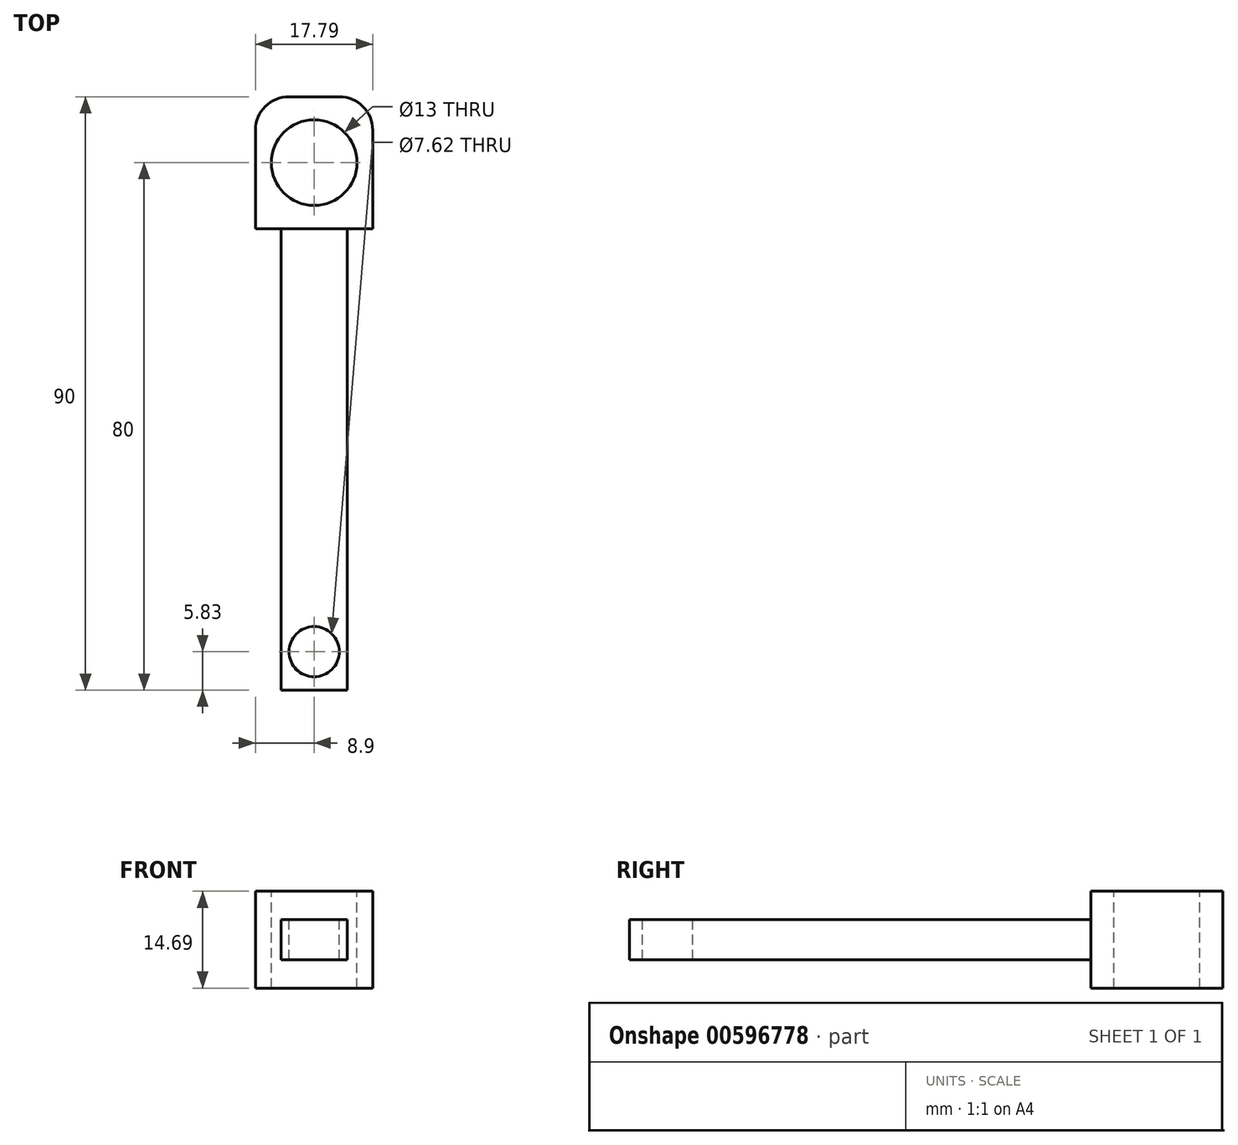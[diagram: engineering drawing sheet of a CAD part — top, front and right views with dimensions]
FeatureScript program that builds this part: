
annotation { "Feature Type Name" : "Feature", "Feature Type Description" : "" }
export const myFeature = defineFeature(function(context is Context, id is Id, definition is map)
    precondition{}
    {
        {
            var Q0;
            Q0=qCreatedBy(makeId("Top.planeOp"),FACE);
            var sketch = newSketch(context, id + "F0", { "sketchPlane" : qUnion([Q0])});
            skLineSegment(sketch, "E0.bottom", {"start": v(5, -35) * mm, "end": v(-5, -35) * mm});
            skLineSegment(sketch, "E0.top", {"start": v(5, 35) * mm, "end": v(-5, 35) * mm});
            skLineSegment(sketch, "E0.left", {"start": v(5, -35) * mm, "end": v(5, 35) * mm});
            skLineSegment(sketch, "E0.right", {"start": v(-5, -35) * mm, "end": v(-5, 35) * mm});
            skPoint(sketch, "E0.middle", {"position": v(0, 0) * mm});
            skPoint(sketch, "E1.firstSnap0", {"position": v(0, 35) * mm});
            skLineSegment(sketch, "E1.bottom", {"start": v(-8.9, 35) * mm, "end": v(8.89, 35) * mm});
            skLineSegment(sketch, "E1.top", {"start": v(-8.9, 55) * mm, "end": v(8.89, 55) * mm});
            skLineSegment(sketch, "E1.left", {"start": v(-8.9, 35) * mm, "end": v(-8.9, 55) * mm});
            skLineSegment(sketch, "E1.right", {"start": v(8.89, 35) * mm, "end": v(8.89, 55) * mm});
            skSolve(sketch);
        }
        {
            var Q0;
            Q0=makeQuery(id+"F0.imprint","IMPRINT",FACE,{"disambiguationData":[TD([[makeQuery(id+"F0.imprint","IMPRINT",EDGE,{"derivedFrom":sQuery(id+"F0.wireOp",EDGE,"E1.top")}),-1.0]])]});
            var Q1;
            Q1=makeQuery(id+"F0.imprint","IMPRINT",FACE,{"disambiguationData":[TD([[makeQuery(id+"F0.imprint","IMPRINT",EDGE,{"derivedFrom":sQuery(id+"F0.wireOp",EDGE,"E0.bottom")}),-1.0]])]});
            extrude(context, id + "F1", {"entities" : qUnion([Q0, Q1]), "depth" : 14.7 * mm, "offsetDistance" : 25.4 * mm});
        }
        {
            var Q0;
            Q0=makeQuery(id+"F1.opExtrude","SWEPT_FACE",FACE,{"disambiguationData":[OSD([sQuery(id+"F0.wireOp",EDGE,"E0.bottom")])]});
            var sketch = newSketch(context, id + "F2", { "sketchPlane" : qUnion([Q0])});
            skLineSegment(sketch, "E2.bottom", {"start": v(-5, 10.4) * mm, "end": v(5, 10.4) * mm});
            skLineSegment(sketch, "E2.top", {"start": v(-5, 4.29) * mm, "end": v(5, 4.29) * mm});
            skLineSegment(sketch, "E2.left", {"start": v(-5, 10.4) * mm, "end": v(-5, 4.29) * mm});
            skLineSegment(sketch, "E2.right", {"start": v(5, 10.4) * mm, "end": v(5, 4.29) * mm});
            skPoint(sketch, "E2.middle", {"position": v(0, 7.34) * mm});
            skPoint(sketch, "E2.middle.positionSnap0", {"position": v(-5, 7.34) * mm});
            skPoint(sketch, "E2.centerSnap0", {"position": v(-5, 7.34) * mm});
            skSolve(sketch);
        }
        {
            var Q0;
            {var subQ0=sQuery(id+"F2.wireOp",EDGE,"E2.bottom");Q0=makeQuery(id+"F2.imprint","IMPRINT",FACE,{"disambiguationData":[TD([[makeQuery(id+"F2.imprint","IMPRINT",EDGE,{"derivedFrom":subQ0}),1.0]])]});}
            var Q1;
            {var subQ0=sQuery(id+"F2.wireOp",EDGE,"E2.top");Q1=makeQuery(id+"F2.imprint","IMPRINT",FACE,{"disambiguationData":[TD([[makeQuery(id+"F2.imprint","IMPRINT",EDGE,{"derivedFrom":subQ0}),-1.0]])]});}
            extrude(context, id + "F3", {"entities" : qUnion([Q0, Q1]), "operationType" : NewBodyOperationType.REMOVE, "oppositeDirection" : true, "depth" : 70 * mm, "offsetDistance" : 25.4 * mm});
        }
        {
            var Q0;
            Q0=makeQuery(id+"F1.opExtrude","CAP_FACE",FACE,{"disambiguationData":[OSD([sQuery(id+"F0.wireOp",EDGE,"E0.bottom"),sQuery(id+"F0.wireOp",EDGE,"E0.left"),sQuery(id+"F0.wireOp",EDGE,"E0.right"),sQuery(id+"F0.wireOp",EDGE,"E1.bottom"),sQuery(id+"F0.wireOp",EDGE,"E1.top"),sQuery(id+"F0.wireOp",EDGE,"E1.left"),sQuery(id+"F0.wireOp",EDGE,"E1.right")])],"isStart":false});
            var sketch = newSketch(context, id + "F4", { "sketchPlane" : qUnion([Q0])});
            skCircle(sketch, "E3", {"center": v(0, 45) * mm, "radius": 5.47 * mm});
            skPoint(sketch, "E3.centerSnap0", {"position": v(-8.9, 45) * mm});
            skSolve(sketch);
        }
        {
            var Q0;
            Q0=sQuery(id+"F4.wireOp",VERTEX,"E3.center");
            var Q1;
            Q1=makeQuery(id+"F1.opExtrude","SWEPT_BODY",BODY,{"disambiguationData":[OSD([sQuery(id+"F0.wireOp",EDGE,"E0.bottom"),sQuery(id+"F0.wireOp",EDGE,"E0.left"),sQuery(id+"F0.wireOp",EDGE,"E0.right"),sQuery(id+"F0.wireOp",EDGE,"E1.bottom"),sQuery(id+"F0.wireOp",EDGE,"E1.top"),sQuery(id+"F0.wireOp",EDGE,"E1.left"),sQuery(id+"F0.wireOp",EDGE,"E1.right")])]});
            hole(context, id + "F5", {"style" : HoleStyle.SIMPLE, "endStyle" : HoleEndStyle.THROUGH, "holeDiameter" : 13 * mm, "majorDiameter" : 6.35 * mm, "isTappedThrough" : true, "tappedDepth" : 12.7 * mm, "tapClearance" : 3, "locations" : qUnion([Q0]), "scope" : qUnion([Q1])});
        }
        {
            var Q0;
            Q0=makeQuery(id+"F1.opExtrude","SWEPT_EDGE",EDGE,{"disambiguationData":[OSD([sQuery(id+"F0.wireOp",EDGE,"E1.top"),sQuery(id+"F0.wireOp",EDGE,"E1.right")])]});
            var Q1;
            Q1=makeQuery(id+"F1.opExtrude","SWEPT_EDGE",EDGE,{"disambiguationData":[OSD([sQuery(id+"F0.wireOp",EDGE,"E1.top"),sQuery(id+"F0.wireOp",EDGE,"E1.left")])]});
            fillet(context, id + "F6", {"entities" : qUnion([Q0, Q1]), "radius" : 5.08 * mm, "tangentPropagation" : true, "allowEdgeOverflow" : false});
        }
        {
            var Q0;
            Q0=makeQuery(id+"F3.boolean.opBoolean","COPY",FACE,{"derivedFrom":makeQuery(id+"F3.opExtrude","SWEPT_FACE",FACE,{"disambiguationData":[OSD([sQuery(id+"F2.wireOp",EDGE,"E2.bottom")])]})});
            var sketch = newSketch(context, id + "F7", { "sketchPlane" : qUnion([Q0])});
            skCircle(sketch, "E4", {"center": v(0, -29.17) * mm, "radius": 3.81 * mm});
            skPoint(sketch, "E4.centerSnap0", {"position": v(0, -35) * mm});
            skSolve(sketch);
        }
        {
            var Q0;
            Q0=sQuery(id+"F7.wireOp",VERTEX,"E4.center");
            var Q1;
            Q1=makeQuery(id+"F1.opExtrude","SWEPT_BODY",BODY,{"disambiguationData":[OSD([sQuery(id+"F0.wireOp",EDGE,"E0.bottom"),sQuery(id+"F0.wireOp",EDGE,"E0.left"),sQuery(id+"F0.wireOp",EDGE,"E0.right"),sQuery(id+"F0.wireOp",EDGE,"E1.bottom"),sQuery(id+"F0.wireOp",EDGE,"E1.top"),sQuery(id+"F0.wireOp",EDGE,"E1.left"),sQuery(id+"F0.wireOp",EDGE,"E1.right")])]});
            hole(context, id + "F8", {"style" : HoleStyle.SIMPLE, "endStyle" : HoleEndStyle.THROUGH, "holeDiameter" : 7.62 * mm, "majorDiameter" : 6.35 * mm, "isTappedThrough" : true, "tappedDepth" : 12.7 * mm, "tapClearance" : 3, "locations" : qUnion([Q0]), "scope" : qUnion([Q1])});
        }
    });
